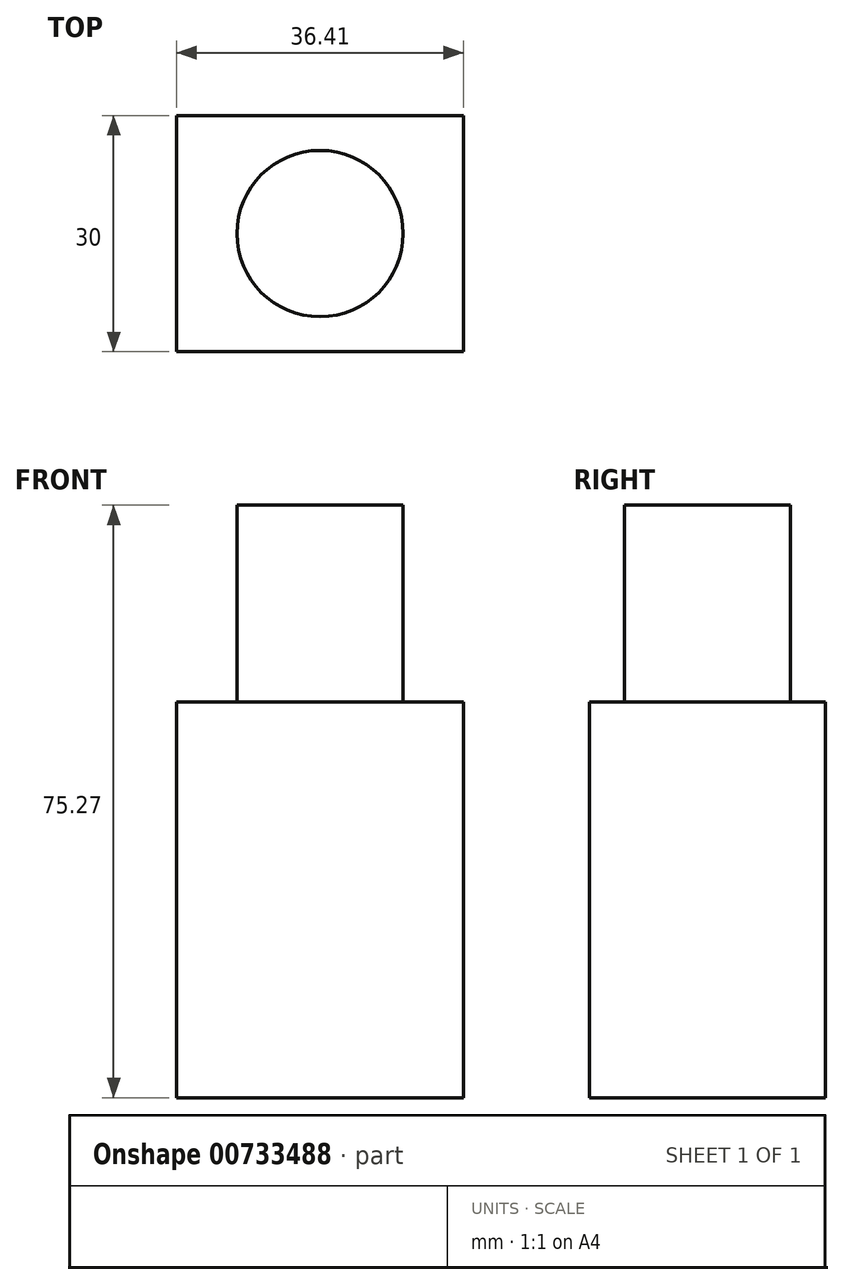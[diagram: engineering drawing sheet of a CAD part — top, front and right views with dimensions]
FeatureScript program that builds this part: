
annotation { "Feature Type Name" : "Feature", "Feature Type Description" : "" }
export const myFeature = defineFeature(function(context is Context, id is Id, definition is map)
    precondition{}
    {
        {
            var Q0;
            Q0=qCreatedBy(makeId("Front.planeOp"),FACE);
            var sketch = newSketch(context, id + "F0", { "sketchPlane" : qUnion([Q0])});
            skLineSegment(sketch, "E0.bottom", {"start": v(0, 0) * mm, "end": v(6.76, 0) * mm});
            skLineSegment(sketch, "E0.top", {"start": v(0, 0) * mm, "end": v(6.76, 0) * mm});
            skLineSegment(sketch, "E0.left", {"start": v(0, 0) * mm, "end": v(0, 0) * mm});
            skLineSegment(sketch, "E0.right", {"start": v(6.76, 0) * mm, "end": v(6.76, 0) * mm});
            skLineSegment(sketch, "E1.bottom", {"start": v(0, 0) * mm, "end": v(36.4, 0) * mm});
            skLineSegment(sketch, "E1.top", {"start": v(0, 50.27) * mm, "end": v(36.4, 50.27) * mm});
            skLineSegment(sketch, "E1.left", {"start": v(0, 0) * mm, "end": v(0, 50.27) * mm});
            skLineSegment(sketch, "E1.right", {"start": v(36.4, 0) * mm, "end": v(36.4, 50.27) * mm});
            skSolve(sketch);
        }
        {
            var Q0;
            Q0 = qSketchRegion(id + "F0", true);
            extrude(context, id + "F1", {"entities" : qUnion([Q0]), "depth" : 30 * mm, "offsetDistance" : 25.4 * mm});
        }
        {
            var Q0;
            Q0=makeQuery(id+"F1.opExtrude","SWEPT_FACE",FACE,{"disambiguationData":[OSD([sQuery(id+"F0.wireOp",EDGE,"E1.top")])]});
            var sketch = newSketch(context, id + "F2", { "sketchPlane" : qUnion([Q0])});
            skCircle(sketch, "E2", {"center": v(18.2, -15) * mm, "radius": 10.56 * mm});
            skPoint(sketch, "E3.orphan", {"position": v(36.4, 0) * mm});
            skPoint(sketch, "E4.start.orphan", {"position": v(0, -30) * mm});
            skSolve(sketch);
        }
        {
            var Q0;
            Q0 = qSketchRegion(id + "F2", true);
            extrude(context, id + "F3", {"entities" : qUnion([Q0]), "operationType" : NewBodyOperationType.ADD, "depth" : 25 * mm, "offsetDistance" : 25 * mm});
        }
    });
